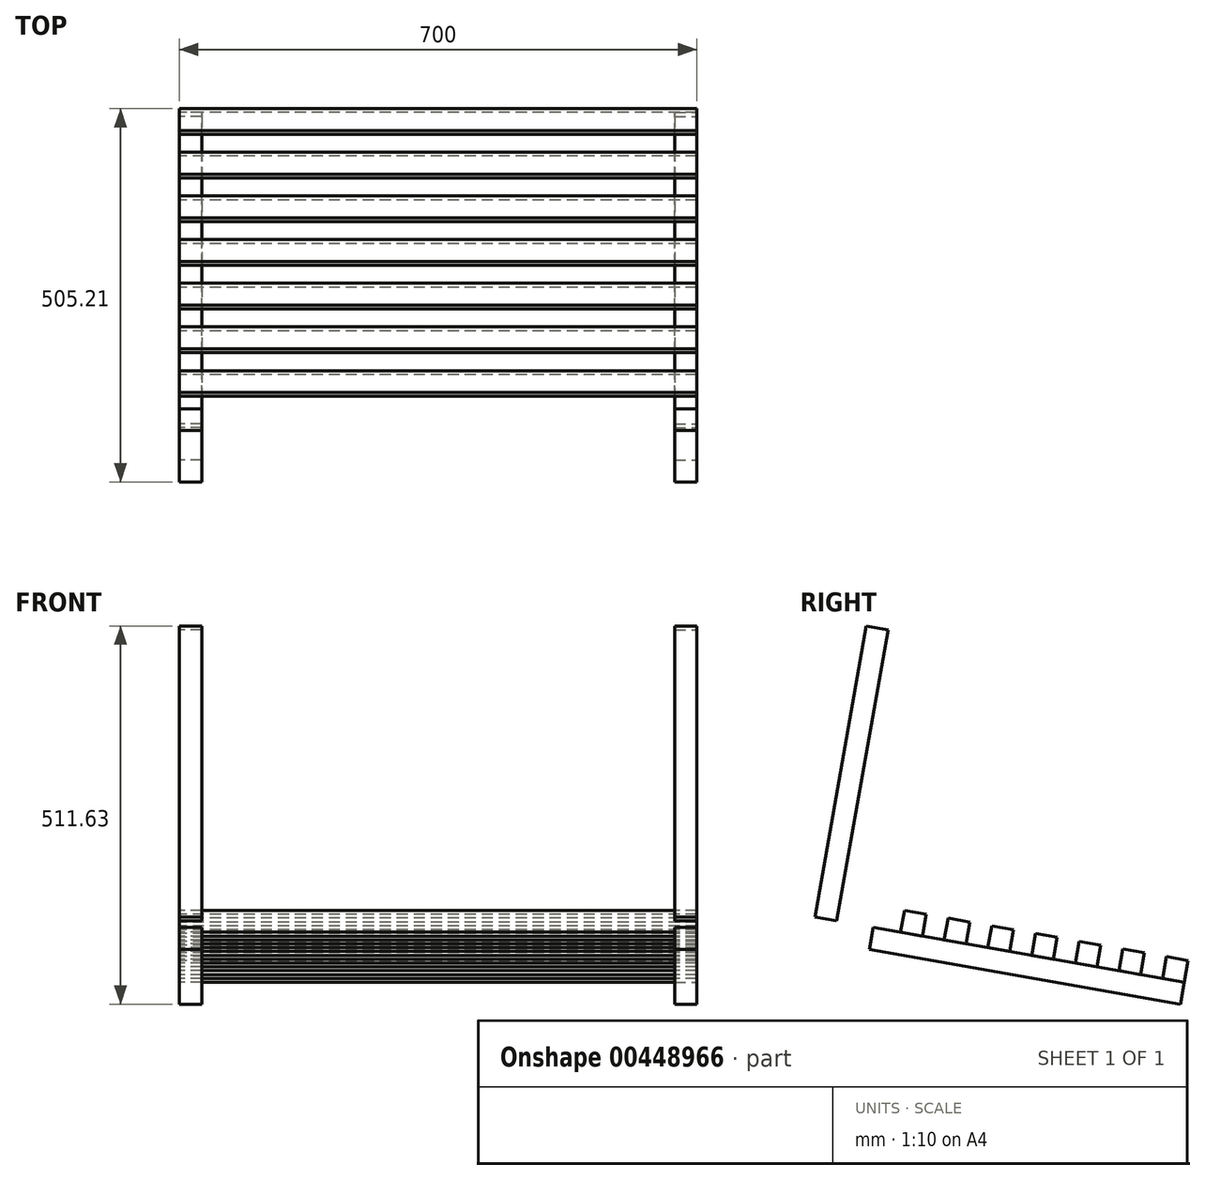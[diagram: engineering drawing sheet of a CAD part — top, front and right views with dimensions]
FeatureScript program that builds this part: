
annotation { "Feature Type Name" : "Feature", "Feature Type Description" : "" }
export const myFeature = defineFeature(function(context is Context, id is Id, definition is map)
    precondition{}
    {
        {
            var Q0;
            Q0=qCreatedBy(makeId("Right.planeOp"),FACE);
            var sketch = newSketch(context, id + "F0", { "sketchPlane" : qUnion([Q0])});
            skLineSegment(sketch, "E0", {"start": v(0, -305.33) * mm, "end": v(0, 525.7) * mm, "construction": true});
            skLineSegment(sketch, "E1", {"start": v(0, 0) * mm, "end": v(500, -88.16) * mm});
            skLineSegment(sketch, "E2", {"start": v(0, 0) * mm, "end": v(69.46, 393.92) * mm});
            skSolve(sketch);
        }
        {
            var Q0;
            Q0=qCreatedBy(makeId("Right.planeOp"),FACE);
            cPlane(context, id + "F1", {"entities" : qUnion([Q0]), "cplaneType" : CPlaneType.OFFSET, "offset" : 350 * mm, "width" : 150 * mm, "height" : 150 * mm});
        }
        {
            var Q0;
            Q0=qCreatedBy(id+"F1.planeOp",FACE);
            cPlane(context, id + "F2", {"entities" : qUnion([Q0]), "cplaneType" : CPlaneType.OFFSET, "offset" : 700 * mm, "oppositeDirection" : true, "width" : 150 * mm, "height" : 150 * mm});
        }
        {
            var Q0;
            Q0=qCreatedBy(id+"F1.planeOp",FACE);
            var sketch = newSketch(context, id + "F3", { "sketchPlane" : qUnion([Q0])});
            skLineSegment(sketch, "E3.0", {"start": v(0, 0) * mm, "end": v(500, -88.16) * mm});
            skLineSegment(sketch, "E4.0", {"start": v(0, 0) * mm, "end": v(69.46, 393.92) * mm});
            skLineSegment(sketch, "E5", {"start": v(500, -88.16) * mm, "end": v(494.8, -117.7) * mm});
            skLineSegment(sketch, "E6", {"start": v(494.8, -117.7) * mm, "end": v(73.58, -43.44) * mm});
            skLineSegment(sketch, "E7", {"start": v(73.58, -43.44) * mm, "end": v(78.78, -13.9) * mm});
            skLineSegment(sketch, "E8", {"start": v(69.46, 393.92) * mm, "end": v(99, 388.71) * mm});
            skLineSegment(sketch, "E9", {"start": v(99, 388.71) * mm, "end": v(29.54, -5.2) * mm});
            skSolve(sketch);
        }
        {
            var Q0;
            Q0=qCreatedBy(id+"F2.planeOp",FACE);
            var sketch = newSketch(context, id + "F4", { "sketchPlane" : qUnion([Q0])});
            skLineSegment(sketch, "E10.0", {"start": v(0, 0) * mm, "end": v(500, -88.16) * mm});
            skLineSegment(sketch, "E10.1", {"start": v(0, 0) * mm, "end": v(69.46, 393.92) * mm});
            skLineSegment(sketch, "E10.2", {"start": v(500, -88.16) * mm, "end": v(494.8, -117.7) * mm});
            skLineSegment(sketch, "E10.3", {"start": v(494.8, -117.7) * mm, "end": v(73.58, -43.44) * mm});
            skLineSegment(sketch, "E10.4", {"start": v(73.58, -43.44) * mm, "end": v(78.78, -13.9) * mm});
            skLineSegment(sketch, "E10.5", {"start": v(69.46, 393.92) * mm, "end": v(99, 388.71) * mm});
            skLineSegment(sketch, "E10.6", {"start": v(99, 388.71) * mm, "end": v(29.54, -5.2) * mm});
            skSolve(sketch);
        }
        {
            var Q0;
            {var subQ0=sQuery(id+"F4.wireOp",EDGE,"E10.2");Q0=makeQuery(id+"F4.imprint","IMPRINT",FACE,{"disambiguationData":[TD([[makeQuery(id+"F4.imprint","IMPRINT",EDGE,{"derivedFrom":subQ0}),-1.0]])]});}
            var Q1;
            {var subQ0=sQuery(id+"F4.wireOp",EDGE,"E10.1");Q1=makeQuery(id+"F4.imprint","IMPRINT",FACE,{"disambiguationData":[TD([[makeQuery(id+"F4.imprint","IMPRINT",EDGE,{"derivedFrom":subQ0}),-1.0]])]});}
            extrude(context, id + "F5", {"entities" : qUnion([Q0, Q1]), "depth" : 30 * mm});
        }
        {
            var Q0;
            {var subQ0=sQuery(id+"F3.wireOp",EDGE,"E4.0");Q0=makeQuery(id+"F3.imprint","IMPRINT",FACE,{"disambiguationData":[TD([[makeQuery(id+"F3.imprint","IMPRINT",EDGE,{"derivedFrom":subQ0}),-1.0]])]});}
            var Q1;
            {var subQ0=sQuery(id+"F3.wireOp",EDGE,"E5");Q1=makeQuery(id+"F3.imprint","IMPRINT",FACE,{"disambiguationData":[TD([[makeQuery(id+"F3.imprint","IMPRINT",EDGE,{"derivedFrom":subQ0}),-1.0]])]});}
            extrude(context, id + "F6", {"entities" : qUnion([Q0, Q1]), "oppositeDirection" : true, "depth" : 30 * mm});
        }
        {
            var Q0;
            Q0=qCreatedBy(makeId("Right.planeOp"),FACE);
            var sketch = newSketch(context, id + "F7", { "sketchPlane" : qUnion([Q0])});
            skLineSegment(sketch, "E11.0", {"start": v(0, 0) * mm, "end": v(500, -88.16) * mm});
            skLineSegment(sketch, "E12", {"start": v(500, -88.16) * mm, "end": v(505.2, -58.62) * mm});
            skLineSegment(sketch, "E13", {"start": v(505.2, -58.62) * mm, "end": v(475.67, -53.4) * mm});
            skLineSegment(sketch, "E14", {"start": v(475.67, -53.4) * mm, "end": v(470.46, -82.95) * mm});
            skLineSegment(sketch, "E15", {"start": v(440.91, -77.74) * mm, "end": v(446.12, -48.2) * mm});
            skLineSegment(sketch, "E16", {"start": v(446.12, -48.2) * mm, "end": v(416.58, -43) * mm});
            skLineSegment(sketch, "E17", {"start": v(416.58, -43) * mm, "end": v(411.37, -72.54) * mm});
            skLineSegment(sketch, "E18", {"start": v(381.82, -67.33) * mm, "end": v(387.03, -37.78) * mm});
            skLineSegment(sketch, "E19", {"start": v(387.03, -37.78) * mm, "end": v(357.49, -32.57) * mm});
            skLineSegment(sketch, "E20", {"start": v(357.49, -32.57) * mm, "end": v(352.28, -62.12) * mm});
            skLineSegment(sketch, "E21", {"start": v(322.73, -56.9) * mm, "end": v(327.94, -27.36) * mm});
            skLineSegment(sketch, "E22", {"start": v(327.94, -27.36) * mm, "end": v(298.4, -22.15) * mm});
            skLineSegment(sketch, "E23", {"start": v(298.4, -22.15) * mm, "end": v(293.2, -51.7) * mm});
            skLineSegment(sketch, "E24", {"start": v(475.67, -53.4) * mm, "end": v(446.12, -48.2) * mm, "construction": true});
            skLineSegment(sketch, "E25", {"start": v(416.58, -43) * mm, "end": v(387.03, -37.78) * mm, "construction": true});
            skLineSegment(sketch, "E26", {"start": v(263.65, -46.49) * mm, "end": v(268.86, -16.94) * mm});
            skLineSegment(sketch, "E27", {"start": v(268.86, -16.94) * mm, "end": v(239.31, -11.73) * mm});
            skLineSegment(sketch, "E28", {"start": v(239.31, -11.73) * mm, "end": v(234.1, -41.28) * mm});
            skLineSegment(sketch, "E29", {"start": v(204.56, -36.07) * mm, "end": v(209.77, -6.52) * mm});
            skLineSegment(sketch, "E30", {"start": v(209.77, -6.52) * mm, "end": v(180.22, -1.32) * mm});
            skLineSegment(sketch, "E31", {"start": v(180.22, -1.32) * mm, "end": v(175.01, -30.86) * mm});
            skLineSegment(sketch, "E32", {"start": v(145.47, -25.65) * mm, "end": v(150.68, 3.9) * mm});
            skLineSegment(sketch, "E33", {"start": v(150.68, 3.9) * mm, "end": v(121.13, 9.1) * mm});
            skLineSegment(sketch, "E34", {"start": v(121.13, 9.1) * mm, "end": v(115.92, -20.44) * mm});
            skLineSegment(sketch, "E35", {"start": v(239.31, -11.73) * mm, "end": v(209.77, -6.52) * mm, "construction": true});
            skLineSegment(sketch, "E36", {"start": v(298.4, -22.15) * mm, "end": v(268.86, -16.94) * mm, "construction": true});
            skSolve(sketch);
        }
        {
            var Q0;
            {var subQ0=sQuery(id+"F7.wireOp",EDGE,"E12");Q0=makeQuery(id+"F7.imprint","IMPRINT",FACE,{"disambiguationData":[TD([[makeQuery(id+"F7.imprint","IMPRINT",EDGE,{"derivedFrom":subQ0}),1.0]])]});}
            var Q1;
            {var subQ0=sQuery(id+"F7.wireOp",EDGE,"E15");Q1=makeQuery(id+"F7.imprint","IMPRINT",FACE,{"disambiguationData":[TD([[makeQuery(id+"F7.imprint","IMPRINT",EDGE,{"derivedFrom":subQ0}),1.0]])]});}
            var Q2;
            {var subQ0=sQuery(id+"F7.wireOp",EDGE,"E18");Q2=makeQuery(id+"F7.imprint","IMPRINT",FACE,{"disambiguationData":[TD([[makeQuery(id+"F7.imprint","IMPRINT",EDGE,{"derivedFrom":subQ0}),1.0]])]});}
            var Q3;
            {var subQ0=sQuery(id+"F7.wireOp",EDGE,"E21");Q3=makeQuery(id+"F7.imprint","IMPRINT",FACE,{"disambiguationData":[TD([[makeQuery(id+"F7.imprint","IMPRINT",EDGE,{"derivedFrom":subQ0}),1.0]])]});}
            var Q4;
            {var subQ0=sQuery(id+"F7.wireOp",EDGE,"E26");Q4=makeQuery(id+"F7.imprint","IMPRINT",FACE,{"disambiguationData":[TD([[makeQuery(id+"F7.imprint","IMPRINT",EDGE,{"derivedFrom":subQ0}),1.0]])]});}
            var Q5;
            {var subQ0=sQuery(id+"F7.wireOp",EDGE,"E29");Q5=makeQuery(id+"F7.imprint","IMPRINT",FACE,{"disambiguationData":[TD([[makeQuery(id+"F7.imprint","IMPRINT",EDGE,{"derivedFrom":subQ0}),1.0]])]});}
            var Q6;
            {var subQ0=sQuery(id+"F7.wireOp",EDGE,"E32");Q6=makeQuery(id+"F7.imprint","IMPRINT",FACE,{"disambiguationData":[TD([[makeQuery(id+"F7.imprint","IMPRINT",EDGE,{"derivedFrom":subQ0}),1.0]])]});}
            var Q7;
            Q7=makeQuery(id+"F6.opExtrude","CAP_FACE",FACE,{"disambiguationData":[OSD([sQuery(id+"F3.wireOp",EDGE,"E3.0"),sQuery(id+"F3.wireOp",EDGE,"E5"),sQuery(id+"F3.wireOp",EDGE,"E6"),sQuery(id+"F3.wireOp",EDGE,"E7")])],"isStart":true});
            var Q8;
            Q8=makeQuery(id+"F5.opExtrude","CAP_FACE",FACE,{"disambiguationData":[OSD([sQuery(id+"F4.wireOp",EDGE,"E10.0"),sQuery(id+"F4.wireOp",EDGE,"E10.2"),sQuery(id+"F4.wireOp",EDGE,"E10.3"),sQuery(id+"F4.wireOp",EDGE,"E10.4")])],"isStart":true});
            extrude(context, id + "F8", {"entities" : qUnion([Q0, Q1, Q2, Q3, Q4, Q5, Q6]), "endBound" : BoundingType.UP_TO_SURFACE, "endBoundEntityFace" : qUnion([Q7]), "depth" : 25 * mm, "hasSecondDirection" : true, "secondDirectionBound" : SecondDirectionBoundingType.UP_TO_SURFACE, "secondDirectionOppositeDirection" : true, "secondDirectionBoundEntityFace" : qUnion([Q8]), "secondDirectionDepth" : 25 * mm});
        }
    });
